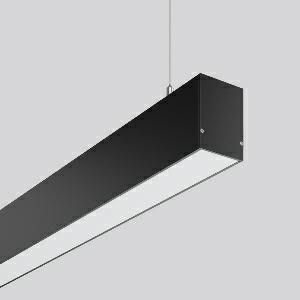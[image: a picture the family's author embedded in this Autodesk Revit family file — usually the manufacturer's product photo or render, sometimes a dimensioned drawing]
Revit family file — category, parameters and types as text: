
# Revit family: less_is_more_50_312314_003_1_8516
name_source: partatom
category: Lighting Fixtures
units: mm (PartAtom-declared; Revit-internal decimal feet)

## family parameters
Cut with Voids When Loaded = No
Host = Face
Light Source = No
Part Type = Normal
Room Calculation Point = No
Round Connector Dimension = Use Diameter
Shared = No

## types (1)
- LESS IS MORE 50 (1 x LED Modul 840, 4850 lm, 4000)
    Apparent Load = 40 VA
    CIE Flux Codes = 48 79 95 100 100
    Color Rendering = 80
    Color Temperature = 4000
    Default Elevation = 1800 mm
    Description = Series: LESS IS MORE 50
Linear pendant luminaire for aesthetically sophisticated lighting. Housing: extruded aluminium profile, powder-coated. End cap aluminium powder-coated. Canopy made of aluminium, powder-coated. Diffuser made of non-yellowing plastic (PMMA), opal. Direct light emission. Suitable for pendant. 2-point steel cable suspension freely positionable and infinitely height-adjustable. Special lengths available on request. LED unit with integrated converter interchangeable and removable. Suitable for through-wiring. With sensors or as a safety luminaire on request. 
Colour: deep black, matt (RAL 9005)
Length: 1687 mm
Width: 57 mm
Height: 75 mm
Suspension length: 2000 mm
Lamp: LED
Socket: without socket
Colour temperature: 4000K
Colour rendering index (CRI): 80
System power: 40 W
Rated luminous flux: 4850 lm
Luminous efficiency: 121 lm/W
Control gear: Regulated power supply
Protection class: I
Type of protection: IP 20
    Height = 75 mm
    Lamp = 1 x LED Modul 840
    Lamp Light Flux = 4850 lm
    Lamp count = 1
    Length = 1687 mm
    Lifetime = 50000 h
    Luminous efficacy = 121 lm/W
    Manufacturer = RZB
    ModVariant = No
    Model = 312314.003.1
    Mounting Place = Ceiling
    Mounting Type = Pendant
    Number of Poles = 1
    OnlyDefault = Yes
    Power Factor = 1
    Product Name = LESS IS MORE 50
    Product group = Pendant LED linear luminaires
    ProductGroupID = 907
    Protection Class = Protection class I
    Protection Degree = IP 20
    RLX_Detail_Level = 1
    RLX_Emergency_Light_Flux = 0 lm
    RLX_Emergency_Type = 0
    RLX_Emergency_Type_DB = No
    RlxData = <blob elided: 28853 chars, md5=eac0f39d>
    Socket = socket
    Standby Power = 0 W
    System Light Flux = 4850 lm
    System Power = 40 W
    Type Comments = Product without accessories
    Type Image = 312318.003.jpg
    URL = http://relux.com
    VarID = ---
    Voltage = 230 V
    Voltage Range = 220-240 V
    Weight = 0.00 kg
    Width = 57 mm

## geometry (parser evidence)
native form markers: Blend x4, Sweep x8
no freeform markers — native parametric forms only
